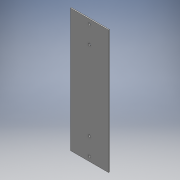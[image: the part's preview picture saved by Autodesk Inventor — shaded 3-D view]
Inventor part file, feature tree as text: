
AUTODESK INVENTOR PART (.ipt)
format: ipt  version: 2016 (Build 200138000, 138)  size: 110,592 bytes
history: native  units: mm
features: extrude x2, sketch x2, other x1
ambient origin geometry x8: Origin, YZ Plane, XZ Plane, XY Plane, X Axis, Y Axis, Z Axis, Center Point
bodies: Body1 (feature_tree)
feature tree (5):
  other  "ソリッド1"
  extrude  "押し出し1"  Depth=80.0mm
  extrude  "押し出し2"  Depth=260.0mm
  sketch  "スケッチ1"
  sketch  "スケッチ2"
